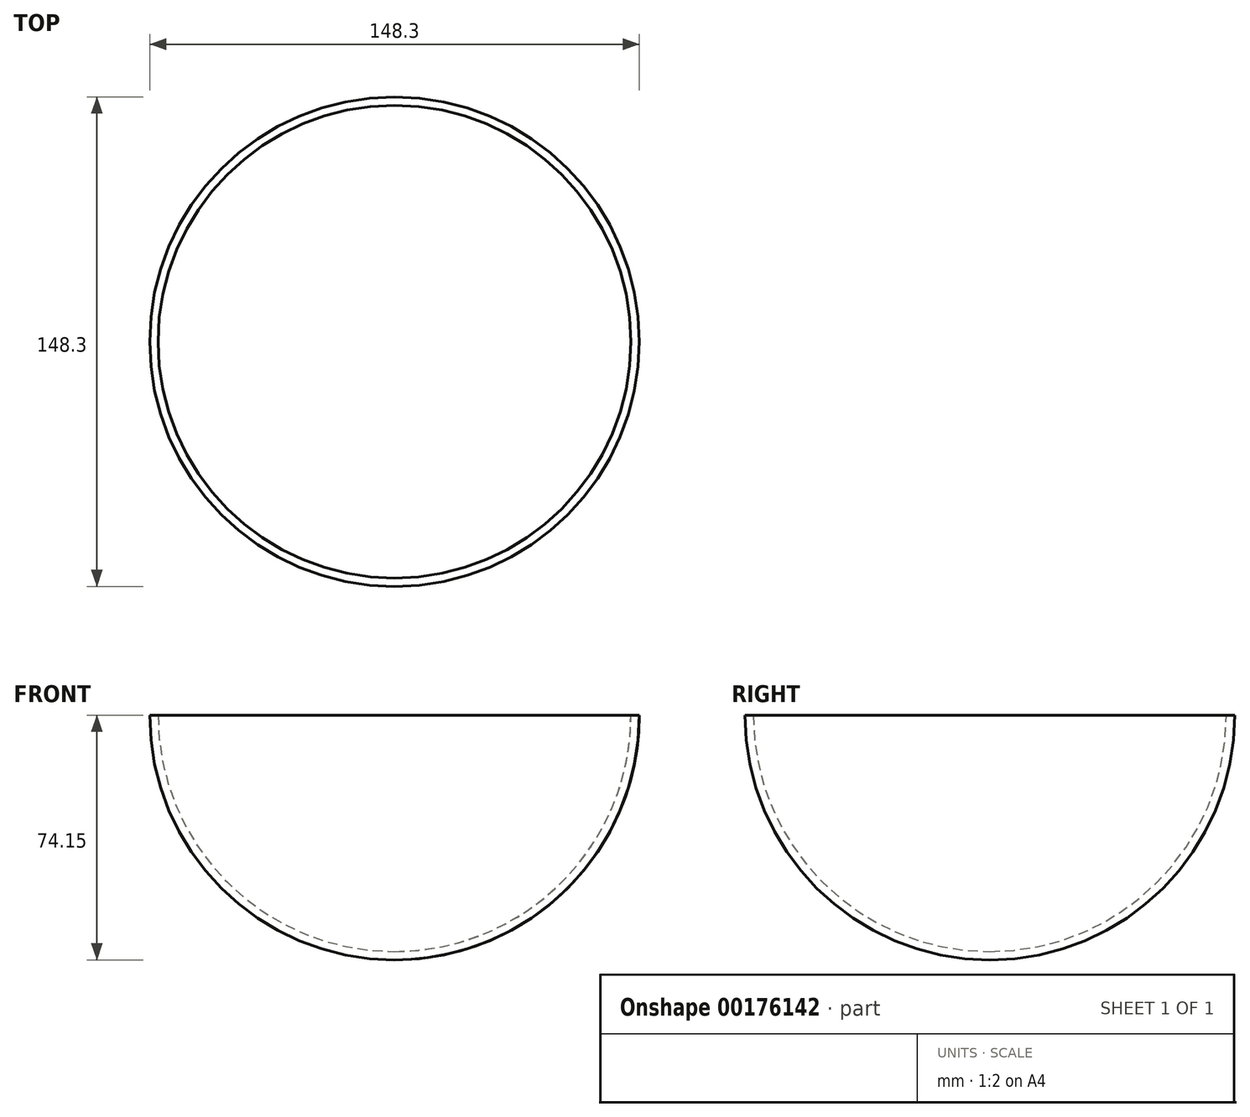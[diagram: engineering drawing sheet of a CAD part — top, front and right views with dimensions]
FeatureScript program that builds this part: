
annotation { "Feature Type Name" : "Feature", "Feature Type Description" : "" }
export const myFeature = defineFeature(function(context is Context, id is Id, definition is map)
    precondition{}
    {
        {
            var Q0;
            Q0=qCreatedBy(makeId("Front.planeOp"),FACE);
            var sketch = newSketch(context, id + "F0", { "sketchPlane" : qUnion([Q0])});
            skLineSegment(sketch, "E0", {"start": v(0, 51.16) * mm, "end": v(0, -23) * mm});
            skArc(sketch, "E1", {"start": v(0, -23) * mm, "mid": v(52.43, -1.28) * mm, "end": v(74.15, 51.16) * mm});
            skLineSegment(sketch, "E2", {"start": v(0, 51.16) * mm, "end": v(74.15, 51.16) * mm});
            skSolve(sketch);
        }
        {
            var Q0;
            Q0=makeQuery(id+"F0.imprint","IMPRINT",FACE,{"disambiguationData":[TD([[makeQuery(id+"F0.imprint","IMPRINT",EDGE,{"derivedFrom":sQuery(id+"F0.wireOp",EDGE,"E0")}),1.0]])]});
            var Q1;
            Q1=sQuery(id+"F0.wireOp",EDGE,"E0");
            revolve(context, id + "F1", {"entities" : qUnion([Q0]), "axis" : qUnion([Q1]), "revolveType" : RevolveType.FULL});
        }
        {
            var Q0;
            Q0=makeQuery(id+"F1.opRevolve","SWEPT_FACE",FACE,{"disambiguationData":[OSD([sQuery(id+"F0.wireOp",EDGE,"E2")])]});
            shell(context, id + "F2", {"entities" : qUnion([Q0]), "thickness" : 2.54 * mm});
        }
    });
